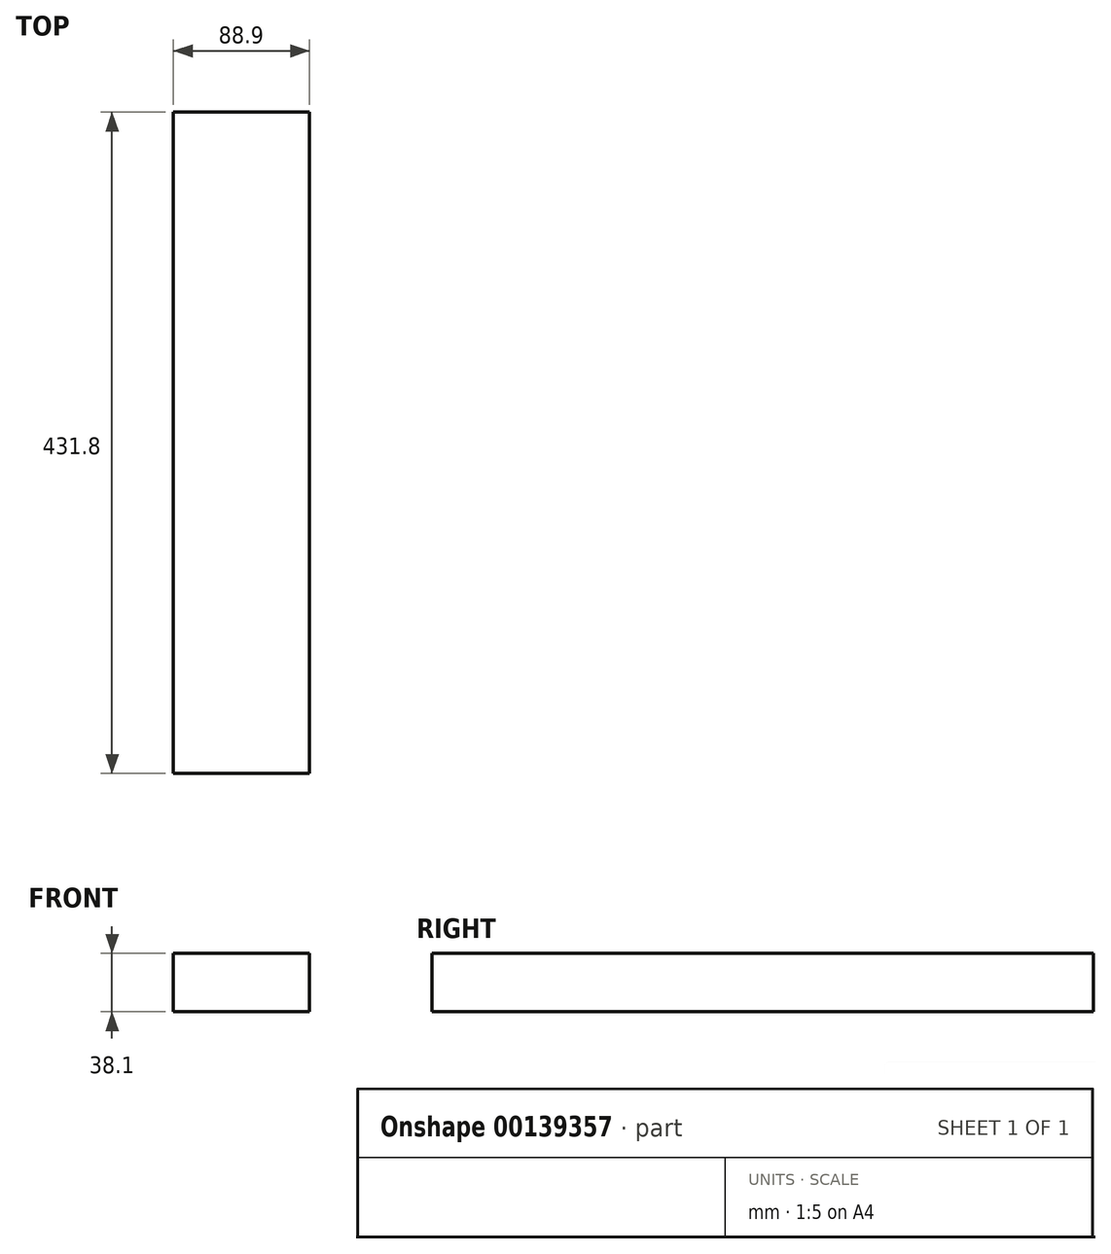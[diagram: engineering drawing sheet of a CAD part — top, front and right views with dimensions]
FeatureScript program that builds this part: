
annotation { "Feature Type Name" : "Feature", "Feature Type Description" : "" }
export const myFeature = defineFeature(function(context is Context, id is Id, definition is map)
    precondition{}
    {
        {
            var Q0;
            Q0=qCreatedBy(makeId("Top.planeOp"),FACE);
            var sketch = newSketch(context, id + "F0", { "sketchPlane" : qUnion([Q0])});
            skLineSegment(sketch, "E0.bottom", {"start": v(44.45, 215.9) * mm, "end": v(-44.45, 215.9) * mm});
            skLineSegment(sketch, "E0.top", {"start": v(44.45, -215.9) * mm, "end": v(-44.45, -215.9) * mm});
            skLineSegment(sketch, "E0.left", {"start": v(44.45, 215.9) * mm, "end": v(44.45, -215.9) * mm});
            skLineSegment(sketch, "E0.right", {"start": v(-44.45, 215.9) * mm, "end": v(-44.45, -215.9) * mm});
            skPoint(sketch, "E0.middle", {"position": v(0, 0) * mm});
            skSolve(sketch);
        }
        {
            var Q0;
            Q0 = qSketchRegion(id + "F0", true);
            extrude(context, id + "F1", {"entities" : qUnion([Q0]), "depth" : 38.1 * mm});
        }
    });
